# Revit family: toilet-floor_mount-zurn-z5635-bwl
name_source: partatom
category: Plumbing Fixtures
units: mm (PartAtom-declared; Revit-internal decimal feet)

## family parameters
Cut with Voids When Loaded = No
Host = Face
Maintain Annotation Orientation = No
OmniClass Number = 23.45.05.21.11.11
OmniClass Title = Water Operated Water Closets
Part Type = Normal
Room Calculation Point = No
Round Connector Dimension = Use Radius
Shared = No

## types (1)
- toilet-floor_mount-zurn-z5635-bwl
    Assembly Code = D2060.10
    CW Connection = No
    CWFU = 0
    Default Elevation = 48 "
    Description = HET Elongated, Floor Mounted Back Outlet EcoVantage® Flush Valve Toilet with Zurn SHIELD™Glaze
    Fixture Mounting Merthod = Floor Mounted
    Flush Rate (GPF) = 1.28
    HW Connection = No
    HWFU = 0
    Height of Bowl = 14 "
    Length of Bowl = 27.375 "
    Main Material = Vitreous China - Zurn - White
    Manufacturer = Zurn Water, LLC
    Manufacturer Brand = Zurn
    Model = Z5635-BWL
    Modified Date = 01/23/2026
    Product Documentation Link = https://files.zurn.com
    Product Page URL = https://www.zurn.com
    Product data URL = https://bimobject.com
    Shipping Weight (lbs) = 65
    URL = https://www.zurn.com
    Vent Connection = No
    WFU = 0
    Waste Connection = Yes
    Width of Bowl = 14.375 "

## geometry (parser evidence)
native form markers: Sweep x5
no freeform markers — native parametric forms only
